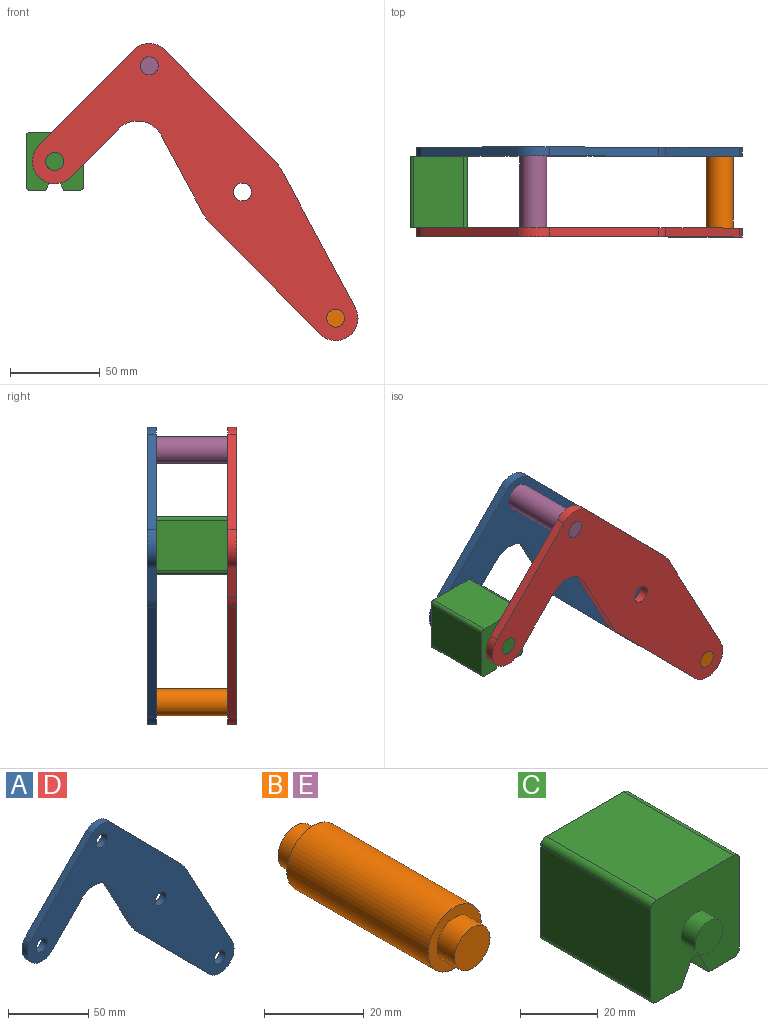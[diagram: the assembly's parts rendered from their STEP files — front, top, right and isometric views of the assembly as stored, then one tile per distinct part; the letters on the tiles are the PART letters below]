
ASSEMBLY  parts=5 mates=3
PART A: 18 faces, bbox 181.7x5x165.8 mm
  f0: plane 43.49x23.35mm, normal (-0.88,0,-0.47), area 246.8mm2, adj f1,f14,f16,f17
  f1: cylinder r=25mm len=5.75mm, axis (0,1,0), area 35.8mm2, adj f0,f2,f16,f17
  f2: plane 61.6x60.87mm, normal (-0.71,0,-0.7), area 433mm2, adj f1,f3,f16,f17
  f3: cylinder r=12.5mm len=21.39mm, axis (0,1,0), area 178.4mm2, adj f2,f4,f16,f17
  f4: plane 76.3x40.96mm, normal (0.88,0,0.47), area 433mm2, adj f3,f5,f16,f17
  f5: cylinder r=25mm len=5.75mm, axis (0,1,0), area 35.8mm2, adj f4,f6,f16,f17
  f6: plane 61.6x60.87mm, normal (0.71,0,0.7), area 433mm2, adj f5,f7,f16,f17
  f7: cylinder r=12.5mm len=17.78mm, axis (0,1,0), area 98.9mm2, adj f6,f8,f16,f17
  f8: plane 53.35x52.71mm, normal (-0.71,0,0.7), area 375mm2, adj f7,f9,f16,f17
  f9: cylinder r=12.5mm len=21.39mm, axis (0,1,0), area 196.3mm2, adj f8,f10,f16,f17
  f10: plane 26.86x26.54mm, normal (0.71,0,-0.7), area 188.8mm2, adj f9,f14,f16,f17
  f11: cylinder r=5mm len=10mm, axis (0,1,0), area 157.1mm2, adj f16,f17
  f12: cylinder r=5mm len=10mm, axis (0,1,0), area 157.1mm2, adj f16,f17
  f13: cylinder r=5mm len=10mm, axis (0,1,0), area 157.1mm2, adj f16,f17
  f14: cylinder r=15mm len=23.89mm, axis (0,1,0), area 140.2mm2, adj f0,f10,f16,f17
  f15: cylinder r=5mm len=10mm, axis (0,1,0), area 157.1mm2, adj f16,f17
  f16: plane 181.66x165.78mm, normal (0,-1,0), area 8710.1mm2, adj f0,f1,f2,f3,f4,f5,f6,f7
  f17: plane 181.66x165.78mm, normal (0,1,0), area 8710.1mm2, adj f0,f1,f2,f3,f4,f5,f6,f7
PART B: 7 faces, bbox 15x50x15 mm
  f0: cylinder r=7.5mm len=40mm, axis (0,-1,0), area 1885mm2, adj f2,f5
  f1: cylinder r=5mm len=10mm, axis (0,1,0), area 157.1mm2, adj f2,f3
  f2: plane 15x15mm, normal (0,-1,0), area 98.2mm2, adj f0,f1
  f3: plane 10x10mm, normal (0,-1,0), area 78.5mm2, adj f1
  f4: cylinder r=5mm len=10mm, axis (0,-1,0), area 157.1mm2, adj f5,f6
  f5: plane 15x15mm, normal (0,1,0), area 98.2mm2, adj f0,f4
  f6: plane 10x10mm, normal (0,1,0), area 78.5mm2, adj f4
PART C: 18 faces, bbox 32.1x50x32.1 mm
  f0: plane 40x28.08mm, normal (1,0,0), area 1123.1mm2, adj f4,f10,f13,f14
  f1: plane 40x9.04mm, normal (0,0,-1), area 361.6mm2, adj f2,f4,f10,f14
  f2: plane 40x6.42mm, normal (-0.89,0,-0.45), area 287.2mm2, adj f1,f4,f10,f15
  f3: plane 40x6.42mm, normal (0.89,0,-0.45), area 287.2mm2, adj f4,f5,f10,f15
  f4: plane 32.08x32.08mm, normal (0,-1,0), area 900.6mm2, adj f0,f1,f2,f3,f5,f6,f7,f9
  f5: plane 40x9.04mm, normal (0,0,-1), area 361.6mm2, adj f3,f4,f10,f16
  f6: plane 40x28.08mm, normal (0,0,1), area 1123.1mm2, adj f4,f10,f13,f17
  f7: plane 40x28.08mm, normal (-1,0,0), area 1123.1mm2, adj f4,f10,f16,f17
  f8: plane 10x10mm, normal (0,-1,0), area 78.5mm2, adj f9
  f9: cylinder r=5mm len=10mm, axis (0,1,0), area 157.1mm2, adj f4,f8
  f10: plane 32.08x32.08mm, normal (0,1,0), area 900.6mm2, adj f0,f1,f2,f3,f5,f6,f7,f12
  f11: plane 10x10mm, normal (0,1,0), area 78.5mm2, adj f12
  f12: cylinder r=5mm len=10mm, axis (0,-1,0), area 157.1mm2, adj f10,f11
  f13: cylinder r=2mm len=40mm, axis (0,1,0), area 125.7mm2, adj f0,f4,f6,f10
  f14: cylinder r=2mm len=40mm, axis (0,-1,0), area 125.7mm2, adj f0,f1,f4,f10
  f15: cylinder r=2mm len=40mm, axis (0,1,0), area 177.1mm2, adj f2,f3,f4,f10
  f16: cylinder r=2mm len=40mm, axis (0,1,0), area 125.7mm2, adj f4,f5,f7,f10
  f17: cylinder r=2mm len=40mm, axis (0,-1,0), area 125.7mm2, adj f4,f6,f7,f10
PART D: same geometry as A
PART E: same geometry as B
PLACE A t=(0,25,0)mm
PLACE B t=(103.95,-20,-140.78)mm
PLACE C t=(0,-20,0)mm
PLACE D t=(0,-20,0)mm fixed
PLACE E t=(0,-20,0)mm
MATE revolute C.f9 <-> D.f9  axis (0,-1,0) through (-104.69,-20,17.04)mm
MATE fastened A.f7 <-> E.f0  axis (0,-1,0) through (-51.98,20,70.39)mm
MATE fastened B.f0 <-> A.f3  axis (0,1,0) through (51.98,20,-70.39)mm
